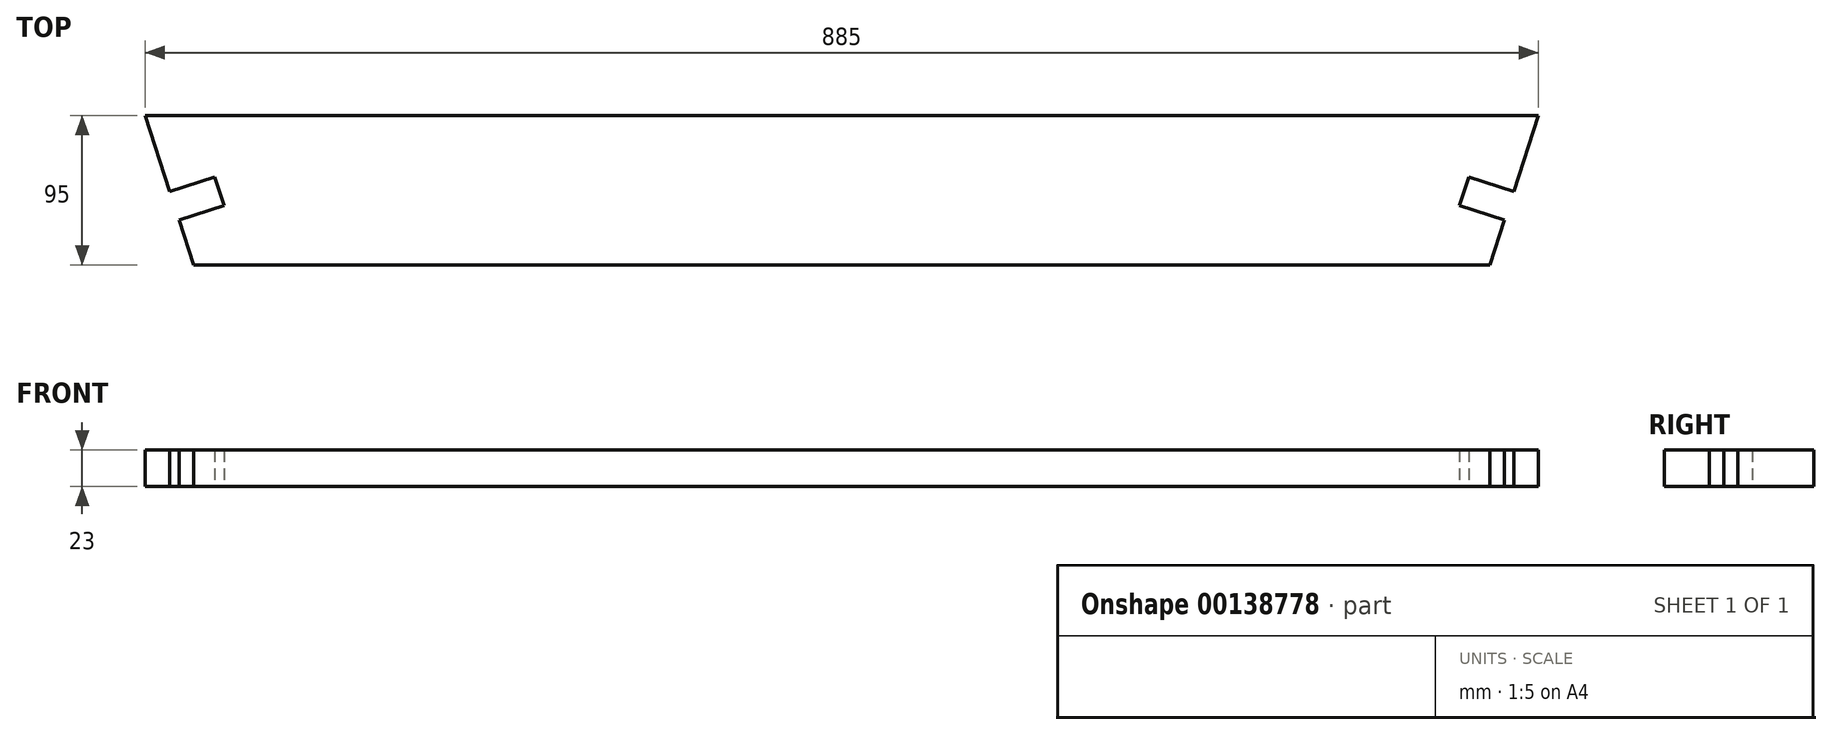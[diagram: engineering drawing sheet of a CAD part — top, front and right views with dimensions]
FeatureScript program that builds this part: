
annotation { "Feature Type Name" : "Feature", "Feature Type Description" : "" }
export const myFeature = defineFeature(function(context is Context, id is Id, definition is map)
    precondition{}
    {
        {
            var Q0;
            Q0=qCreatedBy(makeId("Top.planeOp"),FACE);
            var sketch = newSketch(context, id + "F0", { "sketchPlane" : qUnion([Q0])});
            skLineSegment(sketch, "E0", {"start": v(-442.5, 95) * mm, "end": v(-426.77, 46.6) * mm});
            skLineSegment(sketch, "E1", {"start": v(-426.77, 46.6) * mm, "end": v(-398.24, 55.87) * mm});
            skLineSegment(sketch, "E2", {"start": v(-398.24, 55.87) * mm, "end": v(-392.37, 37.8) * mm});
            skLineSegment(sketch, "E3", {"start": v(-392.37, 37.8) * mm, "end": v(-420.9, 28.53) * mm});
            skLineSegment(sketch, "E4.trimOffspring", {"start": v(-420.9, 28.53) * mm, "end": v(-411.63, 0) * mm});
            skLineSegment(sketch, "E5.MirrorCS", {"start": v(392.37, 37.8) * mm, "end": v(420.9, 28.53) * mm});
            skLineSegment(sketch, "E6.MirrorCS", {"start": v(398.24, 55.87) * mm, "end": v(392.37, 37.8) * mm});
            skLineSegment(sketch, "E7.MirrorCS", {"start": v(426.77, 46.6) * mm, "end": v(398.24, 55.87) * mm});
            skLineSegment(sketch, "E8.MirrorCS", {"start": v(420.9, 28.53) * mm, "end": v(411.63, 0) * mm});
            skLineSegment(sketch, "E9.MirrorCS", {"start": v(442.5, 95) * mm, "end": v(426.77, 46.6) * mm});
            skLineSegment(sketch, "E10", {"start": v(-411.63, 0) * mm, "end": v(411.63, 0) * mm});
            skLineSegment(sketch, "E11", {"start": v(-442.5, 95) * mm, "end": v(442.5, 95) * mm});
            skSolve(sketch);
        }
        {
            var Q0;
            Q0 = qSketchRegion(id + "F0", true);
            extrude(context, id + "F1", {"entities" : qUnion([Q0]), "endBound" : BoundingType.SYMMETRIC, "depth" : 23 * mm});
        }
    });
